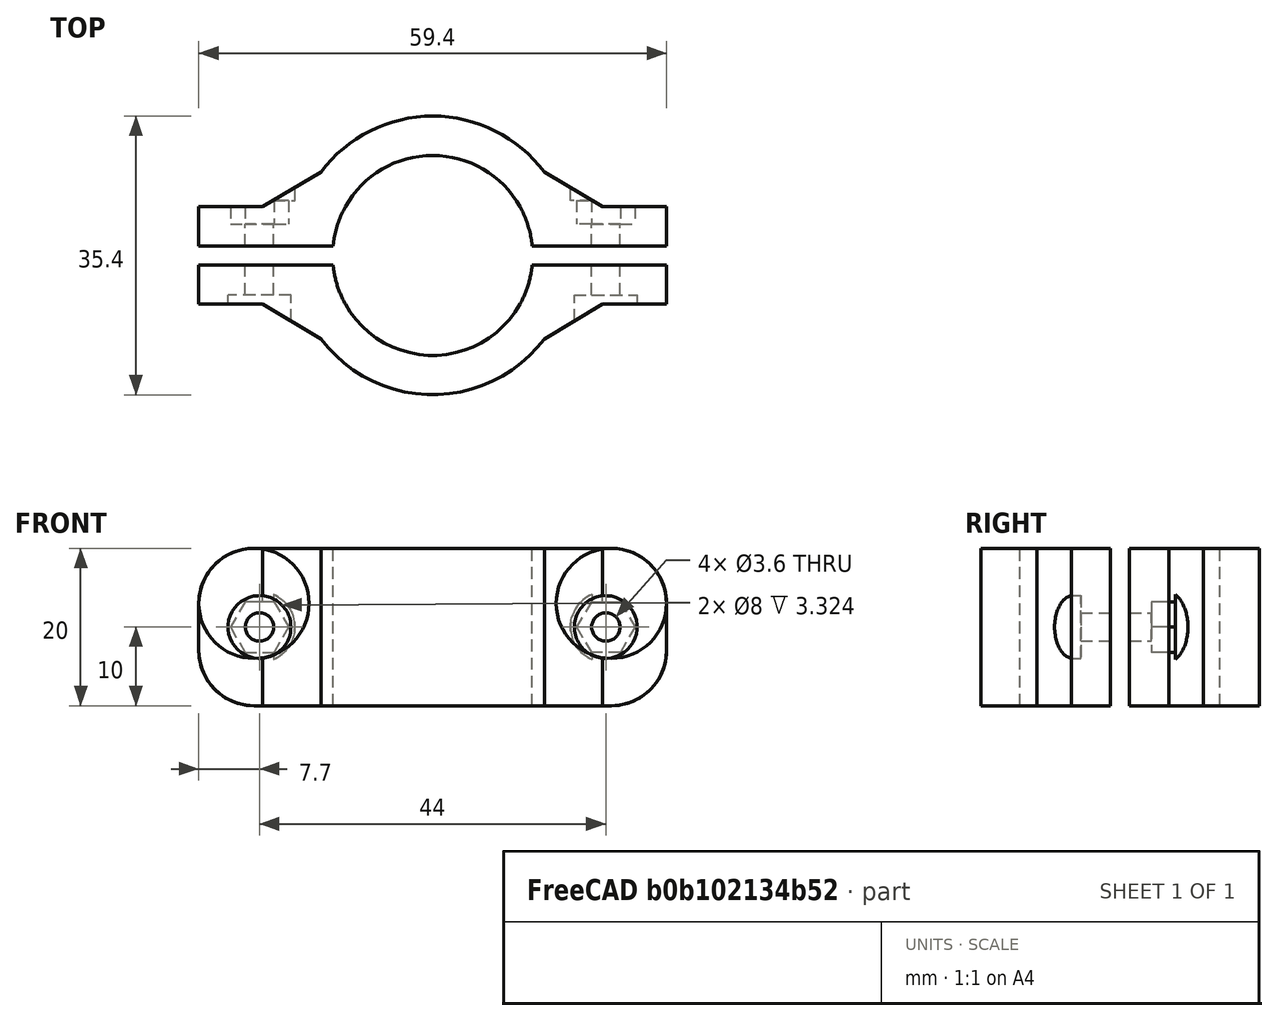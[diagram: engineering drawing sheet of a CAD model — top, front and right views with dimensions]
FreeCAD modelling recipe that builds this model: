
FCSTD DOCUMENT  (FreeCAD 0.18.4R)
Label: pipe_attach
License: All rights reserved
LicenseURL: http://en.wikipedia.org/wiki/All_rights_reserved
objects: Part::Cylinder×5, Part::MultiFuse×4, PartDesign::FeatureBase×2, PartDesign::Body×2, Part::Cut×2, Part::Mirroring×2, App::Part×1, Spreadsheet::Sheet×1, Part::Extrusion×1, Part::Box×1, Part::Fillet×1, Part::Chamfer×1
note: 21 computed .brp shape members not serialized (recipe doc carries the construction recipe); baked Part::Feature solids carry a one-line shape summary decoded from their .brp

FEATURE [App::Part] Part  label="pipe attach part"
  Origin = -> Origin
FEATURE [Spreadsheet::Sheet] Spreadsheet  label="p"
  cells = A1=pipe_r; B1(pipe_r)=12.7; A2=corner_wall; B2(corner_wall)=5; A3=cube_wall_sz; B3(cube_wall_sz)==2 * pipe_r + 2 * corner_wall; A4=cube_extra_axis_sz; B4(cube_extra_axis_sz)=20; A5=cube_cut_along_sz; B5(cube_cut_along_sz)=2.4; A6=cube_cut_across_sz; B6(cube_cut_across_sz)=30; A7=bolt_squeeze_wall; B7(bolt_squeeze_wall)=5; A8=bolt_squeeze_height; B8(bolt_squeeze_height)=12; A9=profile_10x20_hole_width; B9(profile_10x20_hole_width)=10; A10=profile_10x20_hole_length; B10(profile_10x20_hole_length)=20; A11=cube_profile_width; B11(cube_profile_width)=10; A12=cube_profile_length; B12(cube_profile_length)=20; A13=cube_profile_attachment_height; B13(cube_profile_attachment_height)=40; A14=wall; B14(wall)=3; A15=cube_profile_attachment_length; B15(cube_profile_attachment_length)=16; A16=blocker_circumference; B16(blocker_circumference)==p.pipe_r * 2 * pi; A17=blocker_r; B17(blocker_r)==p.pipe_r; A18=blocker_angle; B18(blocker_angle)==p.blocker_circumference / (p.blocker_r * 2 * pi / 360) - 30
FEATURE [Part::Extrusion] Extrude004  label="m3 nut hole001"
  Dir = (0,0,1)
  DirMode = 2
  FaceMakerClass = Part::FaceMakerBullseye
  LengthFwd = 20
  LengthRev = 0
  Solid = true
  Symmetric = false
FEATURE [PartDesign::FeatureBase] Clone036
  BaseFeature = -> Extrude004
FEATURE [PartDesign::Body] Body038  label="m3 nut hole clone004"
  BaseFeature = -> Extrude004
  Group = -> [Clone036]
  Origin = -> Origin061
  Placement = pos=(0,42,0) rot=(1,0,0;1.5708rad)
  Tip = -> Clone036
FEATURE [Part::Cylinder] Cylinder094  label="m3 bolt hole004"
  Angle = 360
  AttacherType = Attacher::AttachEngine3D
  Height = 30
  Placement = pos=(0,0,0) rot=(-1,0,0;1.5708rad)
  Radius = 1.8
FEATURE [Part::Cylinder] Cylinder095  label="bolt head cylinder006"
  Angle = 360
  AttacherType = Attacher::AttachEngine3D
  Height = 20
  Placement = pos=(0,-7,4.9e-15) rot=(-1,0,0;1.5708rad)
  Radius = 4
  expr: Placement.Base.y = 2 - 2 - 2 - p.bolt_squeeze_wall
FEATURE [Part::Cylinder] Cylinder096  label="outer wall001"
  Angle = 160
  AttacherType = Attacher::AttachEngine3D
  Height = 20
  Placement = pos=(0,0,0) rot=(0,0,1;0.174533rad)
  Radius = 17.7
  expr: Radius = p.pipe_r + p.corner_wall
FEATURE [Part::Cylinder] Cylinder097  label="pile extraction001"
  Angle = 360
  AttacherType = Attacher::AttachEngine3D
  Height = 20
  Placement = pos=(0,0,0) rot=(0,0,1;0.174533rad)
  Radius = 12.7
  expr: Radius = p.pipe_r
FEATURE [Part::Box] Box047  label="Cube004"
  AttacherType = Attacher::AttachEngine3D
  Height = 20
  Length = 59.4
  Placement = pos=(-29.7,1.2,0) rot=(0,0,1;0rad)
  Width = 5
  expr: Placement.Base.y = p.cube_cut_along_sz / 2
  expr: Placement.Base.x = -(p.pipe_r + p.corner_wall + p.bolt_squeeze_height)
  expr: Length = (p.pipe_r + p.corner_wall + p.bolt_squeeze_height) * 2
  expr: Width = p.bolt_squeeze_wall
FEATURE [Part::Fillet] Fillet022
  Base = -> Box047
  Edges = 4 edges r=7: [Edge2,Edge4,Edge6,Edge8]
FEATURE [Part::MultiFuse] Fusion072
  Shapes = -> [Cylinder096,Fillet022]
FEATURE [Part::Cut] Cut023016
  Base = -> Fusion072
  Tool = -> Cylinder097
FEATURE [Part::Chamfer] Chamfer004
  Base = -> Cut023016
  Edges = 2 edges r=5: [Edge20,Edge30]
FEATURE [Part::Mirroring] Part__Mirroring005  label="Cut003 (Mirror #2)001"
  Base = (0,2.86102e-06,10)
  Normal = (0,1,-1.19209e-07)
  Source = -> Chamfer004
FEATURE [Part::MultiFuse] Fusion073
  Shapes = -> [Part__Mirroring005,Chamfer004]
FEATURE [Part::Cylinder] Cylinder098  label="nut cylinder001"
  Angle = 360
  AttacherType = Attacher::AttachEngine3D
  Height = 20
  Placement = pos=(0,25,1.9e-14) rot=(-1,0,0;1.5708rad)
  Radius = 4.5
FEATURE [Part::MultiFuse] Fusion071  label="m3 bolt nut fusion006"
  Shapes = -> [Cylinder094,Body038,Cylinder095,Cylinder098]
FEATURE [PartDesign::FeatureBase] Clone037
  BaseFeature = -> Fusion071
FEATURE [PartDesign::Body] Body039  label="m3 bolt nut fusion clone003"
  BaseFeature = -> Fusion071
  Group = -> [Clone037]
  Origin = -> Origin062
  Placement = pos=(-22,0,10) rot=(0,0,1;0rad)
  Tip = -> Clone037
FEATURE [Part::Mirroring] Part__Mirroring006  label="m3 bolt nut fusion clone002 (Mirror #3)001"
  Base = (9.53674e-07,17.5,10)
  Normal = (1,0,-1.19209e-07)
  Source = -> Body039
FEATURE [Part::MultiFuse] Fusion074  label="m3 bolt nut fusion007"
  Placement = pos=(0,-18,0) rot=(0,0,1;0rad)
  Shapes = -> [Part__Mirroring006,Body039]
FEATURE [Part::Cut] Cut023015  label="tube block cut001"
  Base = -> Fusion073
  Tool = -> Fusion074
